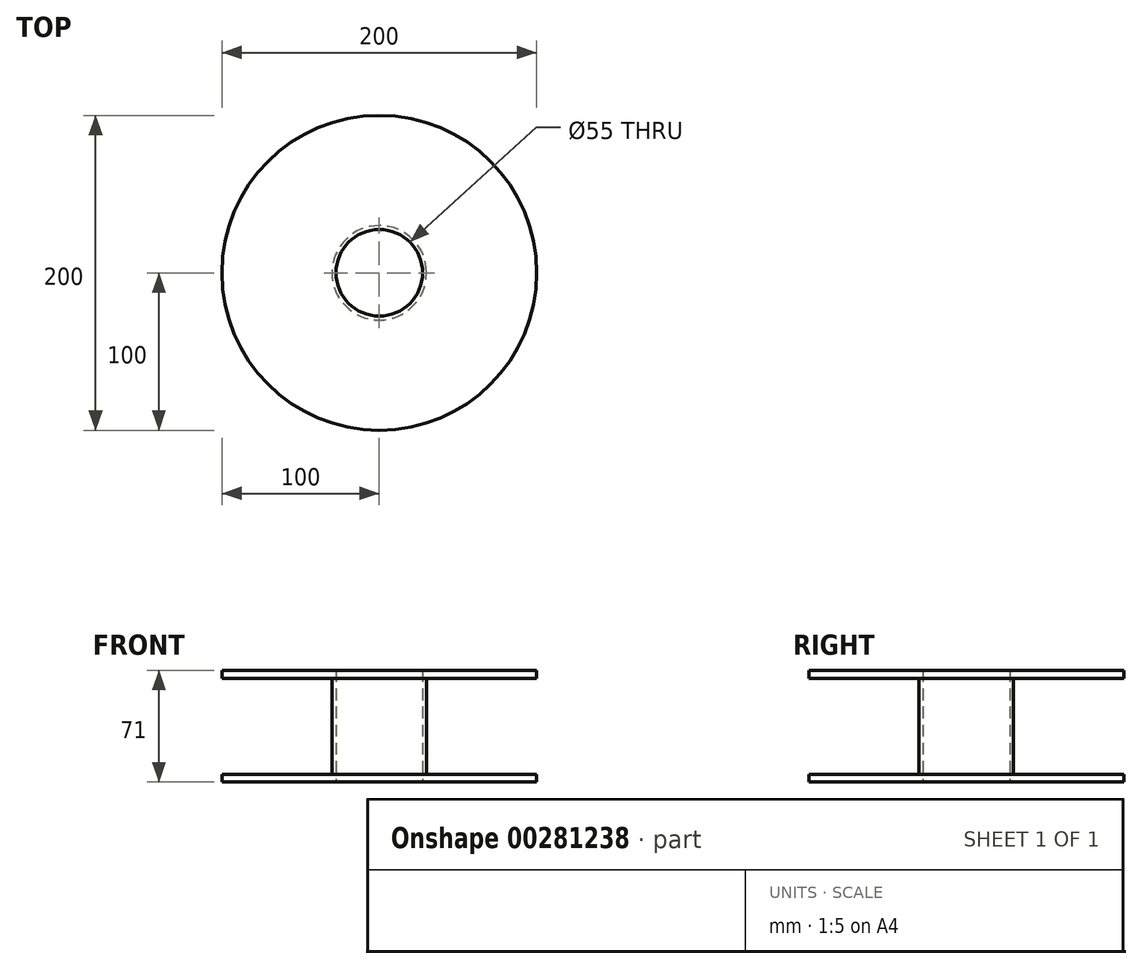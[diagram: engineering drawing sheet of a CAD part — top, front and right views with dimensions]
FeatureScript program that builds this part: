
annotation { "Feature Type Name" : "Feature", "Feature Type Description" : "" }
export const myFeature = defineFeature(function(context is Context, id is Id, definition is map)
    precondition{}
    {
        {
            var Q0;
            Q0=qCreatedBy(makeId("Top.planeOp"),FACE);
            var sketch = newSketch(context, id + "F0", { "sketchPlane" : qUnion([Q0])});
            skCircle(sketch, "E0", {"center": v(0, 0) * mm, "radius": 100 * mm});
            skCircle(sketch, "E1", {"center": v(0, 0) * mm, "radius": 30 * mm});
            skCircle(sketch, "E2", {"center": v(0, 0) * mm, "radius": 27.5 * mm});
            skSolve(sketch);
        }
        {
            var Q0;
            Q0=qSketchRegion(id+"F0",true);
            extrude(context, id + "F1", {"entities" : qUnion([Q0]), "depth" : 5 * mm});
        }
        {
            var Q0;
            Q0=makeQuery(id+"F0.imprint","IMPRINT",FACE,{"disambiguationData":[TD([[makeQuery(id+"F0.imprint","IMPRINT",EDGE,{"derivedFrom":sQuery(id+"F0.wireOp",EDGE,"E1")}),1.0]])]});
            extrude(context, id + "F2", {"entities" : qUnion([Q0]), "operationType" : NewBodyOperationType.ADD, "depth" : 5 * mm, "hasSecondDirection" : true, "secondDirectionOppositeDirection" : true, "secondDirectionDepth" : 66 * mm});
        }
        {
            var Q0;
            Q0=makeQuery(id+"F0.imprint","IMPRINT",FACE,{"disambiguationData":[TD([[makeQuery(id+"F0.imprint","IMPRINT",EDGE,{"derivedFrom":sQuery(id+"F0.wireOp",EDGE,"E0")}),1.0]])]});
            extrude(context, id + "F3", {"entities" : qUnion([Q0]), "operationType" : NewBodyOperationType.ADD, "oppositeDirection" : true, "depth" : 66 * mm, "hasSecondDirection" : true, "secondDirectionOppositeDirection" : true, "secondDirectionDepth" : 61 * mm});
        }
    });
